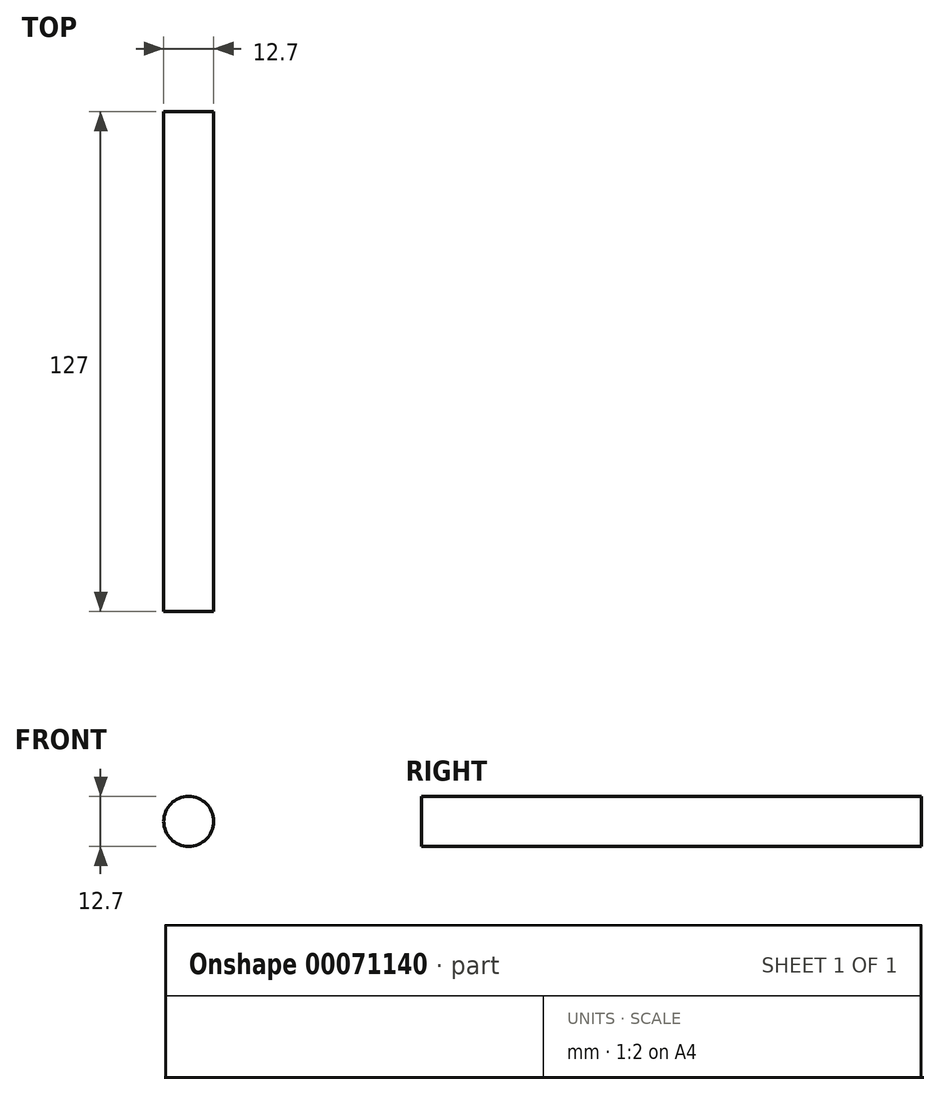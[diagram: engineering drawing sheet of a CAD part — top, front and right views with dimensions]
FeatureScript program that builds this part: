
annotation { "Feature Type Name" : "Feature", "Feature Type Description" : "" }
export const myFeature = defineFeature(function(context is Context, id is Id, definition is map)
    precondition{}
    {
        {
            var Q0;
            Q0=qCreatedBy(makeId("Front.planeOp"),FACE);
            var sketch = newSketch(context, id + "F0", { "sketchPlane" : qUnion([Q0])});
            skCircle(sketch, "E0", {"center": v(-3.03, 11.27) * mm, "radius": 6.35 * mm});
            skSolve(sketch);
        }
        {
            var Q0;
            Q0=makeQuery(id+"F0.imprint","IMPRINT",FACE,{"disambiguationData":[TD([[makeQuery(id+"F0.imprint","IMPRINT",EDGE,{"derivedFrom":sQuery(id+"F0.wireOp",EDGE,"E0")}),1.0]])]});
            extrude(context, id + "F1", {"entities" : qUnion([Q0]), "depth" : 127 * mm});
        }
    });
